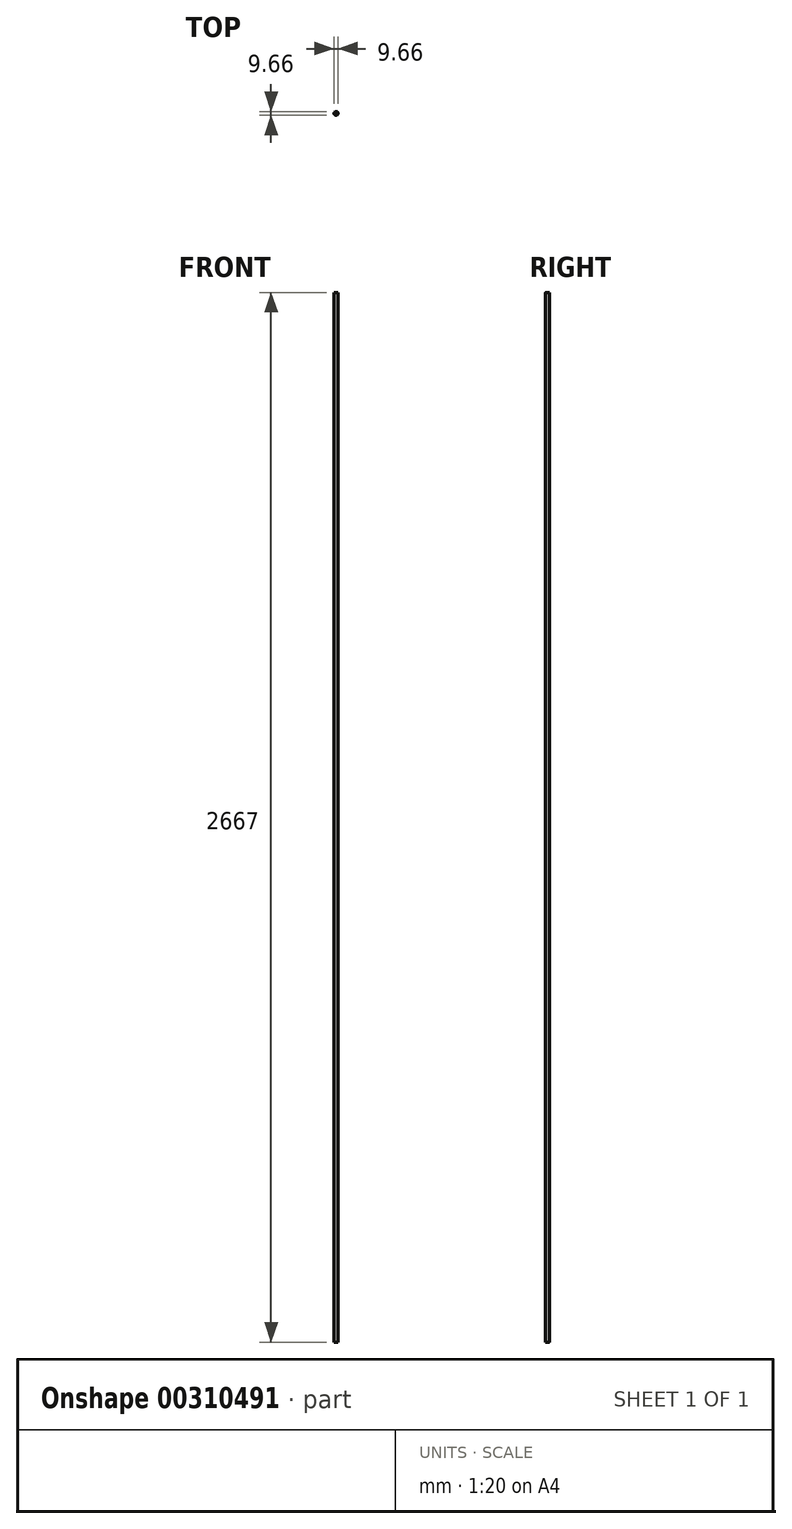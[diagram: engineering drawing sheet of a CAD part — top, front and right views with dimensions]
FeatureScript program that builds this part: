
annotation { "Feature Type Name" : "Feature", "Feature Type Description" : "" }
export const myFeature = defineFeature(function(context is Context, id is Id, definition is map)
    precondition{}
    {
        {
            var Q0;
            Q0=qCreatedBy(makeId("Top.planeOp"),FACE);
            var sketch = newSketch(context, id + "F0", { "sketchPlane" : qUnion([Q0])});
            skCircle(sketch, "E0", {"center": v(0, 0) * mm, "radius": 4.83 * mm});
            skSolve(sketch);
        }
        {
            var Q0;
            Q0=qSketchRegion(id+"F0",true);
            extrude(context, id + "F1", {"entities" : qUnion([Q0]), "endBound" : BoundingType.SYMMETRIC, "depth" : 2667 * mm});
        }
    });
